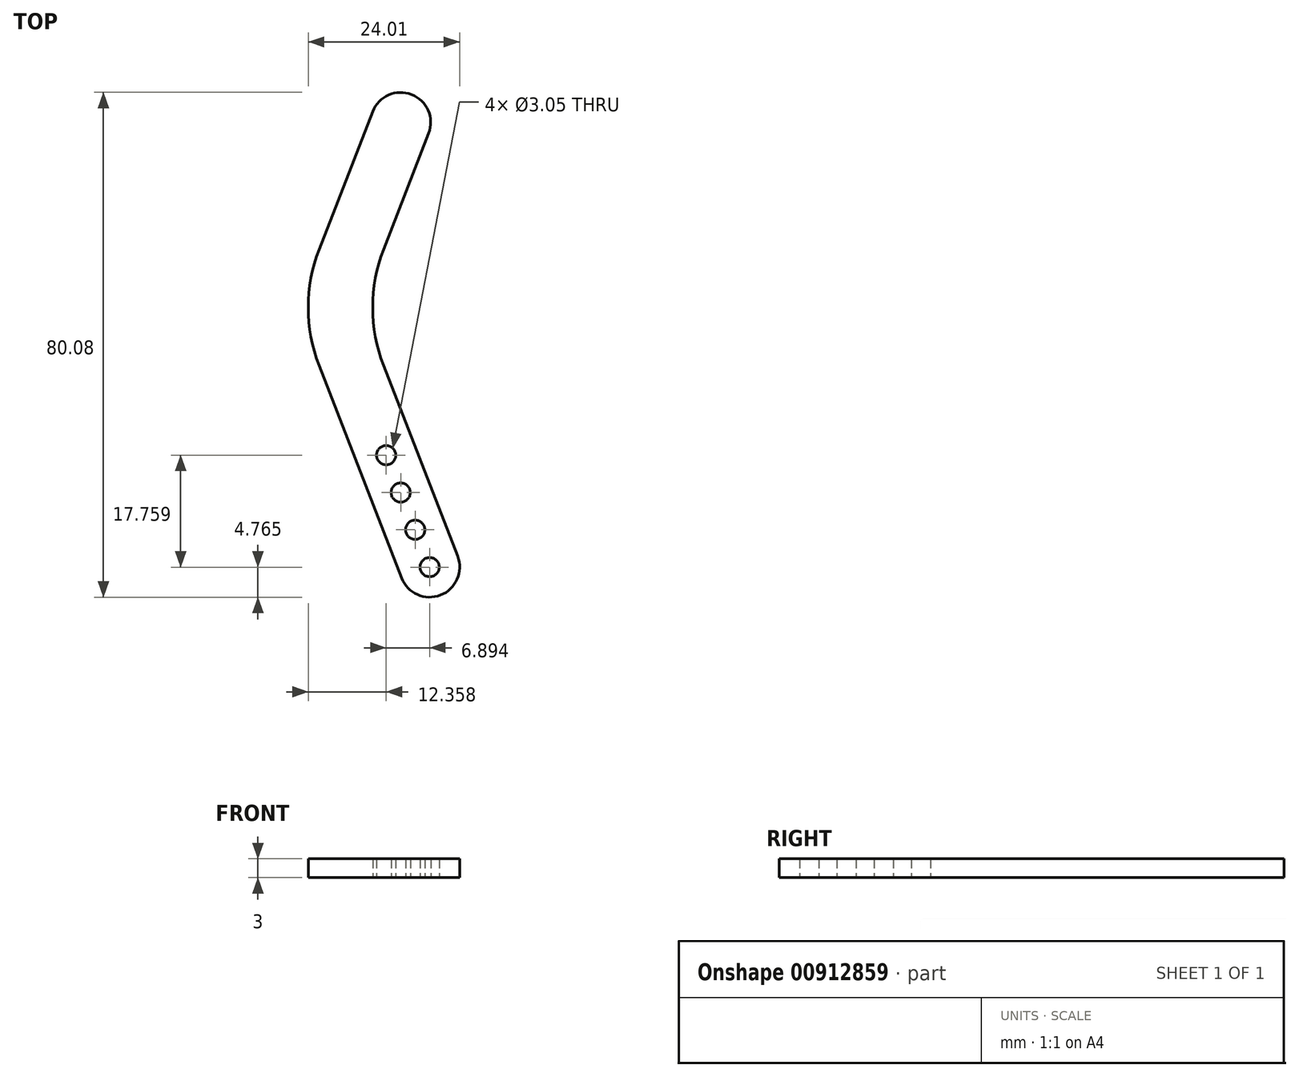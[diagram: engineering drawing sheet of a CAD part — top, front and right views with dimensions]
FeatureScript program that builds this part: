
annotation { "Feature Type Name" : "Feature", "Feature Type Description" : "" }
export const myFeature = defineFeature(function(context is Context, id is Id, definition is map)
    precondition{}
    {
        {
            var Q0;
            Q0=qCreatedBy(makeId("Top.planeOp"),FACE);
            var sketch = newSketch(context, id + "F0", { "sketchPlane" : qUnion([Q0])});
            skLineSegment(sketch, "E0", {"start": v(-24.29, -50.46) * mm, "end": v(-37.38, -16.73) * mm});
            skLineSegment(sketch, "E1", {"start": v(-37.38, 1.65) * mm, "end": v(-28.88, 23.54) * mm});
            skLineSegment(sketch, "E2", {"start": v(-22.72, 26.25) * mm, "end": v(-22.72, 26.25) * mm});
            skLineSegment(sketch, "E3", {"start": v(-20, 20.09) * mm, "end": v(-27.16, 1.65) * mm});
            skLineSegment(sketch, "E4", {"start": v(-27.16, -16.73) * mm, "end": v(-15.4, -47.01) * mm});
            skLineSegment(sketch, "E5", {"start": v(-18.12, -53.17) * mm, "end": v(-18.12, -53.17) * mm});
            skPoint(sketch, "E6.visualSharp", {"position": v(-27.16, 27.98) * mm});
            skArc(sketch, "E6.filletArc", {"start": v(-22.72, 26.25) * mm, "mid": v(-26.36, 26.17) * mm, "end": v(-28.88, 23.54) * mm});
            skPoint(sketch, "E7.visualSharp", {"position": v(-18.28, 24.53) * mm});
            skArc(sketch, "E7.filletArc", {"start": v(-20, 20.09) * mm, "mid": v(-20.09, 23.73) * mm, "end": v(-22.72, 26.25) * mm});
            skPoint(sketch, "E8.visualSharp", {"position": v(-22.56, -54.9) * mm});
            skArc(sketch, "E8.filletArc", {"start": v(-24.29, -50.46) * mm, "mid": v(-21.77, -53.1) * mm, "end": v(-18.12, -53.17) * mm});
            skPoint(sketch, "E9.visualSharp", {"position": v(-13.68, -51.45) * mm});
            skArc(sketch, "E9.filletArc", {"start": v(-18.12, -53.17) * mm, "mid": v(-15.49, -50.66) * mm, "end": v(-15.4, -47.01) * mm});
            skPoint(sketch, "E10.visualSharp", {"position": v(-30.73, -7.54) * mm});
            skArc(sketch, "E10.filletArc", {"start": v(-27.16, 1.65) * mm, "mid": v(-28.88, -7.54) * mm, "end": v(-27.16, -16.73) * mm});
            skPoint(sketch, "E11.visualSharp", {"position": v(-40.95, -7.54) * mm});
            skArc(sketch, "E11.filletArc", {"start": v(-37.38, 1.65) * mm, "mid": v(-39.1, -7.54) * mm, "end": v(-37.38, -16.73) * mm});
            skCircle(sketch, "E12", {"center": v(-19.85, -48.73) * mm, "radius": 1.52 * mm});
            skSolve(sketch);
        }
        {
            var Q0;
            Q0=makeQuery(id+"F0.imprint","IMPRINT",FACE,{"disambiguationData":[TD([[makeQuery(id+"F0.imprint","IMPRINT",EDGE,{"derivedFrom":sQuery(id+"F0.wireOp",EDGE,"E0")}),-1.0]])]});
            extrude(context, id + "F1", {"entities" : qUnion([Q0]), "depth" : 3 * mm, "offsetDistance" : 25.4 * mm});
        }
        {
            var Q0;
            Q0=qCreatedBy(makeId("Top.planeOp"),FACE);
            var sketch = newSketch(context, id + "F2", { "sketchPlane" : qUnion([Q0])});
            skCircle(sketch, "E13", {"center": v(-26.74, -30.98) * mm, "radius": 1.52 * mm});
            skCircle(sketch, "E14", {"center": v(-24.44, -36.9) * mm, "radius": 1.52 * mm});
            skCircle(sketch, "E15", {"center": v(-22.15, -42.82) * mm, "radius": 1.52 * mm});
            skSolve(sketch);
        }
        {
            var Q0;
            Q0 = qSketchRegion(id + "F2", true);
            extrude(context, id + "F3", {"entities" : qUnion([Q0]), "operationType" : NewBodyOperationType.REMOVE, "depth" : 25.4 * mm, "offsetDistance" : 25.4 * mm});
        }
    });
